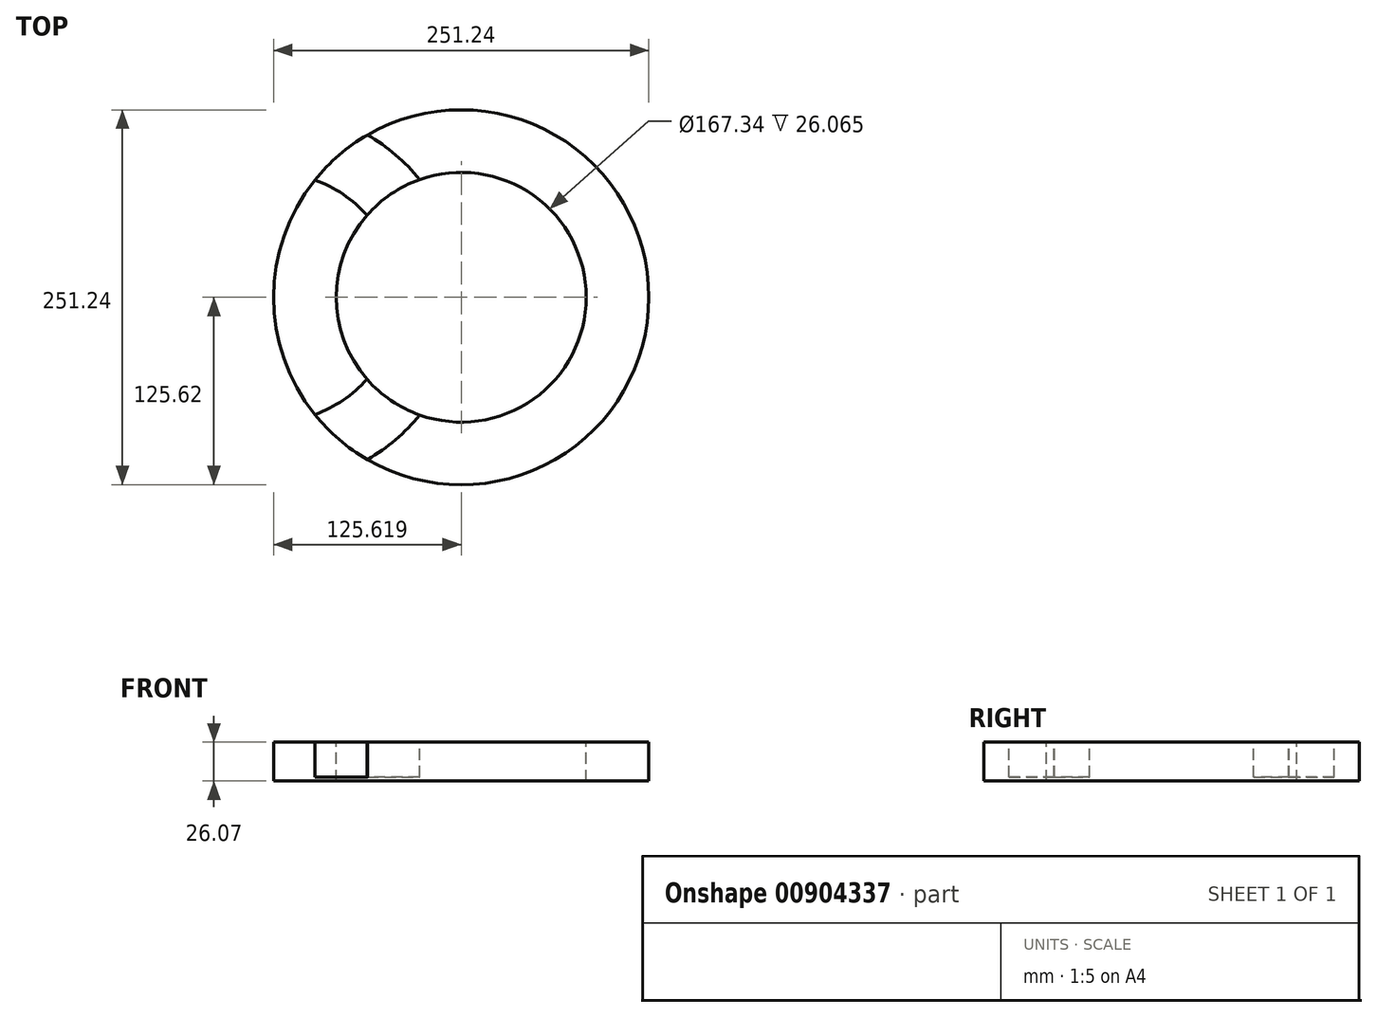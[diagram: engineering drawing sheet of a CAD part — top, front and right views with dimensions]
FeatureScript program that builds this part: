
annotation { "Feature Type Name" : "Feature", "Feature Type Description" : "" }
export const myFeature = defineFeature(function(context is Context, id is Id, definition is map)
    precondition{}
    {
        {
            var Q0;
            Q0=qCreatedBy(makeId("Front.planeOp"),FACE);
            var sketch = newSketch(context, id + "F0", { "sketchPlane" : qUnion([Q0])});
            skLineSegment(sketch, "E0.bottom", {"start": v(-58.17, 6.08) * mm, "end": v(-16.22, 6.08) * mm});
            skLineSegment(sketch, "E0.top", {"start": v(-58.17, -19.99) * mm, "end": v(-16.22, -19.99) * mm});
            skLineSegment(sketch, "E0.left", {"start": v(-58.17, 6.08) * mm, "end": v(-58.17, -19.99) * mm});
            skLineSegment(sketch, "E0.right", {"start": v(-16.22, 6.08) * mm, "end": v(-16.22, -19.99) * mm});
            skLineSegment(sketch, "E1.bottom", {"start": v(25.06, 12.35) * mm, "end": v(67.45, 12.35) * mm});
            skLineSegment(sketch, "E1.top", {"start": v(25.06, -17.36) * mm, "end": v(67.45, -17.36) * mm});
            skLineSegment(sketch, "E1.left", {"start": v(25.06, 12.35) * mm, "end": v(25.06, -17.36) * mm});
            skLineSegment(sketch, "E1.right", {"start": v(67.45, 12.35) * mm, "end": v(67.45, -17.36) * mm});
            skSolve(sketch);
        }
        {
            var Q0;
            Q0=makeQuery(id+"F0.imprint","IMPRINT",FACE,{"disambiguationData":[TD([[makeQuery(id+"F0.imprint","IMPRINT",EDGE,{"derivedFrom":sQuery(id+"F0.wireOp",EDGE,"E0.bottom")}),-1.0]])]});
            var Q1;
            Q1=sQuery(id+"F0.wireOp",EDGE,"E1.right");
            revolve(context, id + "F1", {"surfaceOperationType" : NewSurfaceOperationType.NEW, "entities" : qUnion([Q0]), "axis" : qUnion([Q1]), "revolveType" : RevolveType.FULL});
        }
        {
            var Q0;
            Q0=makeQuery(id+"F0.imprint","IMPRINT",FACE,{"disambiguationData":[TD([[makeQuery(id+"F0.imprint","IMPRINT",EDGE,{"derivedFrom":sQuery(id+"F0.wireOp",EDGE,"E1.bottom")}),-1.0]])]});
            var Q1;
            Q1=sQuery(id+"F0.wireOp",EDGE,"E0.left");
            revolve(context, id + "F2", {"surfaceOperationType" : NewSurfaceOperationType.NEW, "entities" : qUnion([Q0]), "axis" : qUnion([Q1]), "revolveType" : RevolveType.FULL});
        }
        {
            var Q0;
            Q0=makeQuery(id+"F2.opRevolve","SWEPT_BODY",BODY,{"disambiguationData":[OSD([sQuery(id+"F0.wireOp",EDGE,"E1.bottom"),sQuery(id+"F0.wireOp",EDGE,"E1.top"),sQuery(id+"F0.wireOp",EDGE,"E1.left"),sQuery(id+"F0.wireOp",EDGE,"E1.right")])]});
            var Q1;
            Q1=makeQuery(id+"F1.opRevolve","SWEPT_BODY",BODY,{"disambiguationData":[OSD([sQuery(id+"F0.wireOp",EDGE,"E0.bottom"),sQuery(id+"F0.wireOp",EDGE,"E0.top"),sQuery(id+"F0.wireOp",EDGE,"E0.left"),sQuery(id+"F0.wireOp",EDGE,"E0.right")])]});
            booleanBodies(context, id + "F3", {"operationType" : BooleanOperationType.SUBTRACTION, "tools" : qUnion([Q0]), "targets" : qUnion([Q1])});
        }
    });
